# Revit family: Maxlogic akıllı adresli I - O modülleri
name_source: partatom
category: Fire Alarm Devices
units: mm (PartAtom-declared; Revit-internal decimal feet)

## family parameters
Cut with Voids When Loaded = No
Host = Face
Maintain Annotation Orientation = Yes
OmniClass Number = 23.85.30.21
OmniClass Title = Environmental Detection/Registration
Part Type = Normal
Room Calculation Point = No
Round Connector Dimension = Use Diameter
Shared = No

## types (9) — shared parameters
Color = Beyaz
Device Adress Setup = El tipi adresleme cihazı
Fax Number = (+)90 216 466 45 10
Installation Manual = https://mavilielektronik.com
Main Material = White Plastic PC/ABS
Manufacturer = Mavili Elektronik Ticaret A.Ş.
Model = MaxLogic
Mounting surface = Duvara montaj
Nominal Depth = 52 mm
Nominal Height = 100 mm
Nominal Width = 100 mm
Operating temperature = (-10°C) - (+55°C)
Operating voltage range = 18-33V/DC
Operatonal Voltage (default) = 26 V/DC
Secondary Material = Plastic
URL = https://www.mavili.com.tr
Warranty Duration Labor = 2
Warranty Duration Parts = 2
Warranty Duration Unit = Year
Weight = 135 gr
zero-valued in all types: Cost, Default Elevation

## per-type parameters (varying)
| type | Code Performance | Description | Product Code | Public Works Pose Number |
| Maxlogic Adresli röle kontrol modülü, 1 çıkış | EN 54-18 | Adresli röle kontrol modülü, 1 çıkış | ML-1361 | 833-570 |
| Maxlogic Adresli röle kontrol modülü, Kısa Devre İzolatörlü | EN 54-18 | Adresli röle kontrol modülü, Kısa Devre İzolatörlü | ML-1361.SCI | 833-571 |
| Maxlogic Adresli kontak izleme modülü, 1 giriş | EN 54-18 | Adresli kontak izleme modülü, 1 giriş | ML-1362 | 833-575 |
| Maxlogic Adresli kontak izleme modülü, Kısa Devre İzolatörlü | EN 54-18 | Adresli kontak izleme modülü, Kısa Devre İzolatörlü | ML-1362.SCI | 833-576 |
| Maxlogic Adresli 2/1 I/O modül, 2 kontak izleme,1 röle çıkışı | EN 54-18 | Adresli 2/1 I/O modül, 2 kontak izleme,1 röle çıkışı | ML-1363 |  |
| Maxlogic Adresli 2/1 I/O modül, 2 kontak izleme,1 röle çıkışı, Kısa devre izolatörlü | EN 54-18 | Adresli 2/1 I/O modül, 2 kontak izleme,1 röle çıkışı, Kısa Devre İzolatörlü | ML-1363.SCI |  |
| Maxlogic Adresli 4/2 I/O modül, 4 kontak izleme,2 röle çıkışı | EN 54-18 | Adresli 4/2 I/O modül, 4 kontak izleme,2 röle çıkışı | ML-1366 |  |
| Maxlogic Adresli 4/2 I/O modül, 4 kontak izleme,2 röle çıkışı, Kısa devre izolatörlü | EN 54-18 | Adresli 4/2 I/O modül, 4 kontak izleme,2 röle çıkışı, Kısa devre izolatörlü | ML-1366.SCI |  |
| Maxlogic Adresli Sistem Kısa Devre İzolatör Modülü | EN 54-17
EN
54-17 | Adresli Sistem Kısa Devre İzolatör Modülü | ML-1380 | 833-580 |

## geometry (parser evidence)
native form markers: Sweep x1
no freeform markers — native parametric forms only
